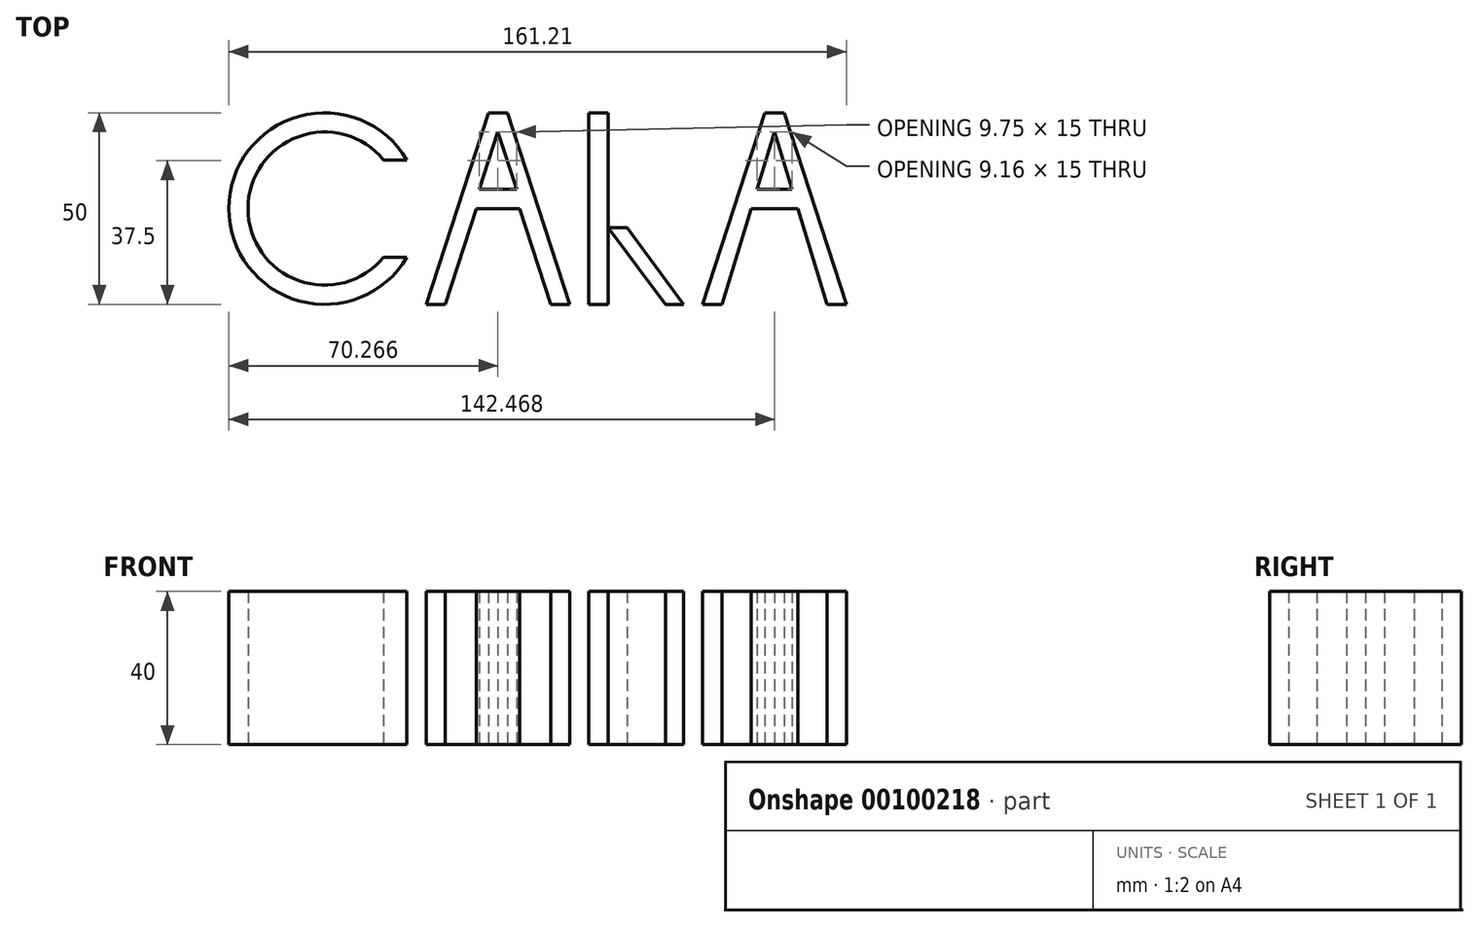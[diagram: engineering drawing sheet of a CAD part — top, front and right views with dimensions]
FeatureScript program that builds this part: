
annotation { "Feature Type Name" : "Feature", "Feature Type Description" : "" }
export const myFeature = defineFeature(function(context is Context, id is Id, definition is map)
    precondition{}
    {
        {
            var Q0;
            Q0=qCreatedBy(makeId("Top.planeOp"),FACE);
            var sketch = newSketch(context, id + "F0", { "sketchPlane" : qUnion([Q0])});
            skArc(sketch, "E0", {"start": v(21.52, 12.72) * mm, "mid": v(-25, 0) * mm, "end": v(21.52, -12.72) * mm});
            skArc(sketch, "E1", {"start": v(15.43, 12.72) * mm, "mid": v(-20, 0) * mm, "end": v(15.43, -12.72) * mm});
            skPoint(sketch, "E2.endSnap0", {"position": v(41.5, -1.23) * mm});
            skLineSegment(sketch, "E3", {"start": v(21.52, 12.72) * mm, "end": v(15.43, 12.72) * mm});
            skLineSegment(sketch, "E4.bottom", {"start": v(18.3, 12.72) * mm, "end": v(21.52, 12.72) * mm});
            skLineSegment(sketch, "E4.top", {"start": v(15.43, -12.72) * mm, "end": v(21.52, -12.72) * mm});
            skLineSegment(sketch, "E5", {"start": v(0, -25) * mm, "end": v(63.04, -25) * mm});
            skPoint(sketch, "E6.end.orphan", {"position": v(34.55, -21.7) * mm});
            skPoint(sketch, "E2.end.orphan", {"position": v(41.5, -5.59) * mm});
            skPoint(sketch, "E7.start.orphan", {"position": v(48.45, 19.22) * mm});
            skLineSegment(sketch, "E8", {"start": v(0, 25) * mm, "end": v(79.01, 25) * mm});
            skLineSegment(sketch, "E9", {"start": v(26.52, -25) * mm, "end": v(42.77, 25) * mm});
            skLineSegment(sketch, "E10", {"start": v(42.77, 25) * mm, "end": v(47.77, 25) * mm});
            skLineSegment(sketch, "E11", {"start": v(47.77, 25) * mm, "end": v(64.01, -25) * mm});
            skLineSegment(sketch, "E12", {"start": v(64.01, -25) * mm, "end": v(59.01, -25) * mm});
            skLineSegment(sketch, "E13", {"start": v(59.01, -25) * mm, "end": v(50.89, 0) * mm});
            skLineSegment(sketch, "E14", {"start": v(39.64, 0) * mm, "end": v(31.52, -25) * mm});
            skLineSegment(sketch, "E15", {"start": v(26.52, -25) * mm, "end": v(31.52, -25) * mm});
            skLineSegment(sketch, "E16", {"start": v(47.77, 25) * mm, "end": v(47.77, 20) * mm});
            skLineSegment(sketch, "E17", {"start": v(45.27, 25) * mm, "end": v(45.27, 20) * mm});
            skLineSegment(sketch, "E18", {"start": v(45.27, 20) * mm, "end": v(40.4, 5) * mm});
            skLineSegment(sketch, "E19", {"start": v(40.4, 5) * mm, "end": v(50.14, 5) * mm});
            skLineSegment(sketch, "E20", {"start": v(50.14, 5) * mm, "end": v(45.27, 20) * mm});
            skLineSegment(sketch, "E21", {"start": v(45.27, 0) * mm, "end": v(45.27, -25) * mm});
            skLineSegment(sketch, "E22", {"start": v(45.27, -25) * mm, "end": v(45.27, 0) * mm});
            skLineSegment(sketch, "E23", {"start": v(45.27, 0) * mm, "end": v(50.89, 0) * mm});
            skLineSegment(sketch, "E24", {"start": v(50.89, 0) * mm, "end": v(39.64, 0) * mm});
            skPoint(sketch, "E25.orphan", {"position": v(45.27, 2.3) * mm});
            skPoint(sketch, "E26.start.orphan", {"position": v(40.4, 2.3) * mm});
            skPoint(sketch, "E27.start.orphan", {"position": v(50.14, 2.3) * mm});
            skLineSegment(sketch, "E28", {"start": v(45.27, 0) * mm, "end": v(45.27, 5) * mm});
            skLineSegment(sketch, "E29", {"start": v(21.52, -12.72) * mm, "end": v(21.52, -25) * mm});
            skLineSegment(sketch, "E30", {"start": v(64.01, -25) * mm, "end": v(69.01, -25) * mm});
            skLineSegment(sketch, "E31.bottom", {"start": v(69.01, -25) * mm, "end": v(74.01, -25) * mm});
            skLineSegment(sketch, "E31.top", {"start": v(69.01, 25) * mm, "end": v(74.01, 25) * mm});
            skPoint(sketch, "E32.end.orphan", {"position": v(74.01, 20) * mm});
            skPoint(sketch, "E32.start.orphan", {"position": v(79.01, 20) * mm});
            skPoint(sketch, "E33.start.orphan", {"position": v(89.01, -25) * mm});
            skPoint(sketch, "E31.right.start.orphan", {"position": v(74.01, 0) * mm});
            skLineSegment(sketch, "E34.left", {"start": v(69.01, -25) * mm, "end": v(69.01, 25) * mm});
            skLineSegment(sketch, "E34.right", {"start": v(74.01, -25) * mm, "end": v(74.01, 25) * mm});
            skLineSegment(sketch, "E35", {"start": v(74.01, 25) * mm, "end": v(79.01, 25) * mm});
            skLineSegment(sketch, "E36", {"start": v(89.01, -25) * mm, "end": v(93.72, -25) * mm});
            skLineSegment(sketch, "E37", {"start": v(74.01, 0) * mm, "end": v(79.01, 0) * mm});
            skPoint(sketch, "E37.endSnap0", {"position": v(55.89, 0) * mm});
            skLineSegment(sketch, "E38", {"start": v(79.01, 5) * mm, "end": v(79.01, 20) * mm});
            skLineSegment(sketch, "E39", {"start": v(74.01, -25) * mm, "end": v(74.01, -5) * mm});
            skLineSegment(sketch, "E40", {"start": v(74.01, -5) * mm, "end": v(89.01, -25) * mm});
            skLineSegment(sketch, "E41", {"start": v(74.01, -5) * mm, "end": v(79.01, -5) * mm});
            skLineSegment(sketch, "E42", {"start": v(79.01, -5) * mm, "end": v(93.72, -25) * mm});
            skArc(sketch, "E43", {"start": v(79.01, -5) * mm, "mid": v(94.01, 10) * mm, "end": v(79.01, 25) * mm});
            skArc(sketch, "E44.0", {"start": v(79.01, 0) * mm, "mid": v(89.01, 10) * mm, "end": v(79.01, 20) * mm});
            skLineSegment(sketch, "E45", {"start": v(79.01, 20) * mm, "end": v(74.01, 20) * mm});
            skLineSegment(sketch, "E46", {"start": v(93.72, -25) * mm, "end": v(98.72, -25) * mm});
            skLineSegment(sketch, "E47", {"start": v(98.72, -25) * mm, "end": v(114.97, 25) * mm});
            skLineSegment(sketch, "E48", {"start": v(114.97, 25) * mm, "end": v(119.97, 25) * mm});
            skLineSegment(sketch, "E49", {"start": v(119.97, 25) * mm, "end": v(136.21, -25) * mm});
            skLineSegment(sketch, "E50", {"start": v(136.21, -25) * mm, "end": v(131.21, -25) * mm});
            skLineSegment(sketch, "E51", {"start": v(98.72, -25) * mm, "end": v(103.72, -25) * mm});
            skLineSegment(sketch, "E52", {"start": v(103.72, -25) * mm, "end": v(131.21, -25) * mm});
            skLineSegment(sketch, "E53", {"start": v(117.47, -25) * mm, "end": v(117.47, 0) * mm});
            skLineSegment(sketch, "E54", {"start": v(117.47, 25) * mm, "end": v(117.47, 20) * mm});
            skLineSegment(sketch, "E55", {"start": v(117.47, 20) * mm, "end": v(103.72, -25) * mm});
            skLineSegment(sketch, "E56", {"start": v(131.21, -25) * mm, "end": v(117.47, 20) * mm});
            skLineSegment(sketch, "E57", {"start": v(117.47, 0) * mm, "end": v(123.58, 0) * mm});
            skLineSegment(sketch, "E58", {"start": v(123.58, 0) * mm, "end": v(111.36, 0) * mm});
            skLineSegment(sketch, "E59", {"start": v(117.47, 0) * mm, "end": v(117.47, 5) * mm});
            skLineSegment(sketch, "E60", {"start": v(117.47, 5) * mm, "end": v(122.05, 5) * mm});
            skLineSegment(sketch, "E61", {"start": v(122.05, 5) * mm, "end": v(112.89, 5) * mm});
            skSolve(sketch);
        }
        {
            var Q0;
            Q0=makeQuery(id+"F0.imprint","IMPRINT",FACE,{"disambiguationData":[TD([[makeQuery(id+"F0.imprint","IMPRINT",EDGE,{"derivedFrom":sQuery(id+"F0.wireOp",EDGE,"E1")}),-1.0]])]});
            var Q1;
            {var subQ2=sQuery(id+"F0.wireOp",EDGE,"E9");Q1=makeQuery(id+"F0.imprint","IMPRINT",FACE,{"disambiguationData":[TD([[makeQuery(id+"F0.imprint","IMPRINT",EDGE,{"derivedFrom":subQ2}),-1.0]])]});}
            var Q2;
            {var subQ4=sQuery(id+"F0.wireOp",EDGE,"E11");Q2=makeQuery(id+"F0.imprint","IMPRINT",FACE,{"disambiguationData":[TD([[makeQuery(id+"F0.imprint","IMPRINT",EDGE,{"derivedFrom":subQ4}),-1.0]])]});}
            var Q3;
            Q3=makeQuery(id+"F0.imprint","IMPRINT",FACE,{"disambiguationData":[TD([[makeQuery(id+"F0.imprint","IMPRINT",EDGE,{"derivedFrom":sQuery(id+"F0.wireOp",EDGE,"E31.bottom")}),1.0]])]});
            var Q4;
            Q4=makeQuery(id+"F0.imprint","IMPRINT",FACE,{"disambiguationData":[TD([[makeQuery(id+"F0.imprint","IMPRINT",EDGE,{"derivedFrom":sQuery(id+"F0.wireOp",EDGE,"E36")}),1.0]])]});
            var Q5;
            {var subQ2=sQuery(id+"F0.wireOp",EDGE,"E35");Q5=makeQuery(id+"F0.imprint","IMPRINT",FACE,{"disambiguationData":[TD([[makeQuery(id+"F0.imprint","IMPRINT",EDGE,{"derivedFrom":subQ2}),-1.0]])]});}
            var Q6;
            {var subQ2=sQuery(id+"F0.wireOp",EDGE,"E47");Q6=makeQuery(id+"F0.imprint","IMPRINT",FACE,{"disambiguationData":[TD([[makeQuery(id+"F0.imprint","IMPRINT",EDGE,{"derivedFrom":subQ2}),-1.0]])]});}
            var Q7;
            {var subQ5=sQuery(id+"F0.wireOp",EDGE,"E59");Q7=makeQuery(id+"F0.imprint","IMPRINT",FACE,{"disambiguationData":[TD([[makeQuery(id+"F0.imprint","IMPRINT",EDGE,{"derivedFrom":subQ5}),1.0]])]});}
            var Q8;
            {var subQ5=sQuery(id+"F0.wireOp",EDGE,"E59");Q8=makeQuery(id+"F0.imprint","IMPRINT",FACE,{"disambiguationData":[TD([[makeQuery(id+"F0.imprint","IMPRINT",EDGE,{"derivedFrom":subQ5}),-1.0]])]});}
            var Q9;
            {var subQ1=sQuery(id+"F0.wireOp",EDGE,"E49");Q9=makeQuery(id+"F0.imprint","IMPRINT",FACE,{"disambiguationData":[TD([[makeQuery(id+"F0.imprint","IMPRINT",EDGE,{"derivedFrom":subQ1}),-1.0]])]});}
            extrude(context, id + "F1", {"entities" : qUnion([Q0, Q1, Q2, Q3, Q4, Q5, Q6, Q7, Q8, Q9]), "depth" : 40 * mm});
        }
    });
